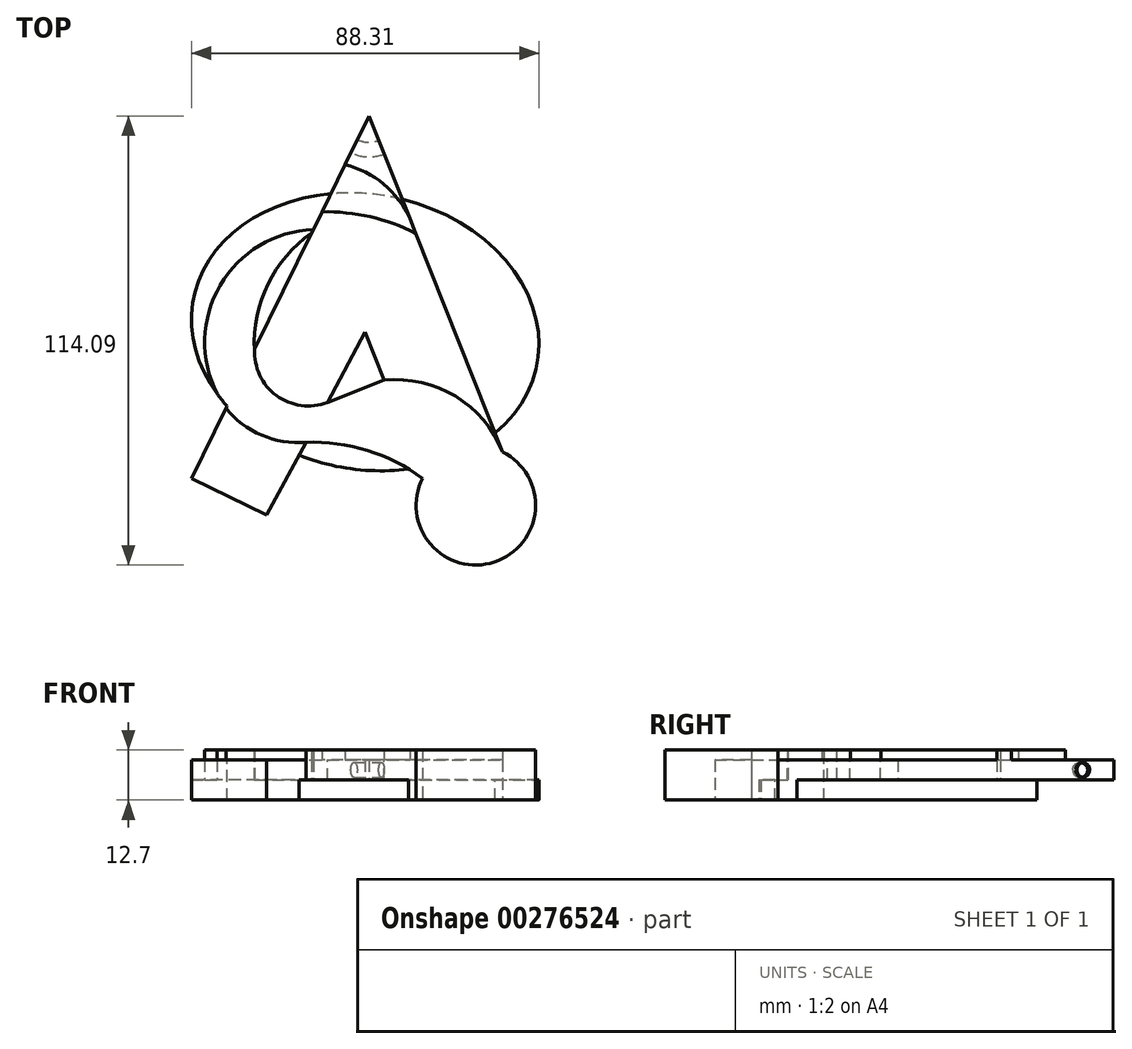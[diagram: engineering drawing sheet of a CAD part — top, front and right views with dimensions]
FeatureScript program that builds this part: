
annotation { "Feature Type Name" : "Feature", "Feature Type Description" : "" }
export const myFeature = defineFeature(function(context is Context, id is Id, definition is map)
    precondition{}
    {
        {
            var Q0;
            Q0=qCreatedBy(makeId("Top.planeOp"),FACE);
            var sketch = newSketch(context, id + "F0", { "sketchPlane" : qUnion([Q0])});
            skEllipse(sketch, "E0", {"center": v(-96.84, -32.47) * mm, "majorRadius": 44.45 * mm, "minorRadius": 34.93 * mm, "majorAxis": v(0.98, -0.19)});
            skSolve(sketch);
        }
        {
            var Q0;
            Q0=makeQuery(id+"F0.imprint","IMPRINT",FACE,{"disambiguationData":[TD([[makeQuery(id+"F0.imprint","IMPRINT",EDGE,{"derivedFrom":sQuery(id+"F0.wireOp",EDGE,"E0")}),1.0]])]});
            extrude(context, id + "F1", {"entities" : qUnion([Q0]), "depth" : 5.08 * mm});
        }
        {
            var Q0;
            Q0=makeQuery(id+"F1.opExtrude","CAP_FACE",FACE,{"disambiguationData":[OSD([sQuery(id+"F0.wireOp",EDGE,"E0")])],"isStart":false});
            var sketch = newSketch(context, id + "F2", { "sketchPlane" : qUnion([Q0])});
            skLineSegment(sketch, "E1", {"start": v(-140.96, -69.67) * mm, "end": v(-95.88, 22.4) * mm});
            skLineSegment(sketch, "E2", {"start": v(-95.88, 22.4) * mm, "end": v(-61.92, -63) * mm});
            skLineSegment(sketch, "E3", {"start": v(-140.96, -69.67) * mm, "end": v(-121.84, -79.03) * mm});
            skLineSegment(sketch, "E4", {"start": v(-121.84, -79.03) * mm, "end": v(-96.84, -32.47) * mm});
            skLineSegment(sketch, "E5", {"start": v(-96.84, -32.47) * mm, "end": v(-82.23, -69.67) * mm});
            skArc(sketch, "E6", {"start": v(-82.23, -69.67) * mm, "mid": v(-64, -90.95) * mm, "end": v(-61.92, -63) * mm});
            skSolve(sketch);
        }
        {
            var Q0;
            {var subQ0=sQuery(id+"F2.wireOp",EDGE,"E3");Q0=makeQuery(id+"F2.imprint","IMPRINT",FACE,{"disambiguationData":[TD([[makeQuery(id+"F2.imprint","IMPRINT",EDGE,{"derivedFrom":subQ0}),1.0]])]});}
            var Q1;
            {var subQ1=makeQuery(id+"F1.opExtrude","CAP_EDGE",EDGE,{"disambiguationData":[OSD([sQuery(id+"F0.wireOp",EDGE,"E0")])],"isStart":false});var subQ4=sQuery(id+"F2.wireOp",EDGE,"E1");var subQ11=makeQuery(id+"F2.imprint","INTERSECT",VERTEX,{"disambiguationData":[OD(0.0)],"derivedFrom":[subQ1,subQ4]});Q1=makeQuery(id+"F2.imprint","IMPRINT",FACE,{"disambiguationData":[TD([[makeQuery(id+"F2.imprint","IMPRINT",EDGE,{"disambiguationData":[TD([[subQ11,-1.0]])],"derivedFrom":subQ4}),-1.0]])]});}
            var Q2;
            {var subQ0=sQuery(id+"F2.wireOp",EDGE,"E6");Q2=makeQuery(id+"F2.imprint","IMPRINT",FACE,{"disambiguationData":[TD([[makeQuery(id+"F2.imprint","IMPRINT",EDGE,{"derivedFrom":subQ0}),1.0]])]});}
            var Q3;
            {var subQ0=sQuery(id+"F2.wireOp",EDGE,"E2");var subQ1=sQuery(id+"F2.wireOp",EDGE,"E1");var subQ2=makeQuery(id+"F2.imprint","INTERSECT",VERTEX,{"derivedFrom":[subQ1,subQ0]});Q3=makeQuery(id+"F2.imprint","IMPRINT",FACE,{"disambiguationData":[TD([[makeQuery(id+"F2.imprint","IMPRINT",EDGE,{"disambiguationData":[TD([[subQ2,1.0]])],"derivedFrom":subQ1}),-1.0]])]});}
            extrude(context, id + "F3", {"entities" : qUnion([Q0, Q1, Q2, Q3]), "operationType" : NewBodyOperationType.ADD, "depth" : 5.08 * mm});
        }
        {
            var Q0;
            Q0=makeQuery(id+"F3.opExtrude","CAP_FACE",FACE,{"disambiguationData":[OSD([sQuery(id+"F2.wireOp",EDGE,"E1"),sQuery(id+"F2.wireOp",EDGE,"E2"),sQuery(id+"F2.wireOp",EDGE,"E3"),sQuery(id+"F2.wireOp",EDGE,"E4"),sQuery(id+"F2.wireOp",EDGE,"E5"),sQuery(id+"F2.wireOp",EDGE,"E6")])],"isStart":false});
            var sketch = newSketch(context, id + "F4", { "sketchPlane" : qUnion([Q0])});
            skArc(sketch, "E7", {"start": v(-61.92, -63) * mm, "mid": v(-73.9, -48.83) * mm, "end": v(-92.01, -44.75) * mm});
            skLineSegment(sketch, "E8", {"start": v(-92.01, -44.75) * mm, "end": v(-106.45, -50.36) * mm});
            skArc(sketch, "E9", {"start": v(-124.88, -36.83) * mm, "mid": v(-119.38, -48.65) * mm, "end": v(-106.45, -50.36) * mm});
            skArc(sketch, "E10", {"start": v(-108.32, -3) * mm, "mid": v(-121.21, -17.66) * mm, "end": v(-124.88, -36.83) * mm});
            skArc(sketch, "E11", {"start": v(-108.32, -3) * mm, "mid": v(-133.14, -21.13) * mm, "end": v(-132.24, -51.85) * mm});
            skArc(sketch, "E12", {"start": v(-132.24, -51.85) * mm, "mid": v(-123.15, -58.72) * mm, "end": v(-111.9, -60.52) * mm});
            skArc(sketch, "E13", {"start": v(-82.23, -69.67) * mm, "mid": v(-96.3, -62.6) * mm, "end": v(-111.9, -60.52) * mm});
            skSolve(sketch);
        }
        {
            var Q0;
            {var subQ0=sQuery(id+"F4.wireOp",EDGE,"E7");Q0=makeQuery(id+"F4.imprint","IMPRINT",FACE,{"disambiguationData":[TD([[makeQuery(id+"F4.imprint","IMPRINT",EDGE,{"derivedFrom":subQ0}),1.0]])]});}
            var Q1;
            {var subQ0=sQuery(id+"F4.wireOp",EDGE,"E8");Q1=makeQuery(id+"F4.imprint","IMPRINT",FACE,{"disambiguationData":[TD([[makeQuery(id+"F4.imprint","IMPRINT",EDGE,{"derivedFrom":subQ0}),1.0]])]});}
            var Q2;
            {var subQ0=sQuery(id+"F4.wireOp",EDGE,"E9");Q2=makeQuery(id+"F4.imprint","IMPRINT",FACE,{"disambiguationData":[TD([[makeQuery(id+"F4.imprint","IMPRINT",EDGE,{"derivedFrom":subQ0}),-1.0]])]});}
            extrude(context, id + "F5", {"entities" : qUnion([Q0, Q1, Q2]), "operationType" : NewBodyOperationType.ADD, "depth" : 2.54 * mm});
        }
        {
            var Q0;
            {var subQ0=sQuery(id+"F0.wireOp",EDGE,"E0");var subQ1=sQuery(id+"F2.wireOp",EDGE,"E1");Q0=makeQuery(id+"F3.boolean.opBoolean","SPLIT",FACE,{"disambiguationData":[TD([makeQuery(id+"F3.opExtrude","SWEPT_FACE",FACE,{"disambiguationData":[OSD([subQ1])]})])],"derivedFrom":makeQuery(id+"F1.opExtrude","CAP_FACE",FACE,{"disambiguationData":[OSD([subQ0])],"isStart":false})});}
            var sketch = newSketch(context, id + "F6", { "sketchPlane" : qUnion([Q0])});
            skArc(sketch, "E14", {"start": v(-110.02, -6.47) * mm, "mid": v(-134.67, -22.53) * mm, "end": v(-132.24, -51.85) * mm});
            skArc(sketch, "E15", {"start": v(-110.45, -7.36) * mm, "mid": v(-121.54, -20.36) * mm, "end": v(-125, -37.08) * mm});
            skSolve(sketch);
        }
        {
            var Q0;
            Q0=makeQuery(id+"F5.opExtrude","CAP_FACE",FACE,{"disambiguationData":[OSD([sQuery(id+"F2.wireOp",EDGE,"E1"),sQuery(id+"F2.wireOp",EDGE,"E6"),sQuery(id+"F4.wireOp",EDGE,"E7"),sQuery(id+"F4.wireOp",EDGE,"E8"),sQuery(id+"F4.wireOp",EDGE,"E9"),sQuery(id+"F4.wireOp",EDGE,"E12"),sQuery(id+"F4.wireOp",EDGE,"E13")])],"isStart":true});
            extrude(context, id + "F7", {"entities" : qUnion([Q0]), "operationType" : NewBodyOperationType.ADD, "depth" : 10.16 * mm});
        }
        {
            var Q0;
            {var subQ0=sQuery(id+"F2.wireOp",EDGE,"E3");var subQ1=sQuery(id+"F0.wireOp",EDGE,"E0");var subQ2=sQuery(id+"F2.wireOp",EDGE,"E1");var subQ3=sQuery(id+"F2.wireOp",EDGE,"E4");Q0=makeQuery(id+"F3.boolean.opBoolean","SPLIT",FACE,{"disambiguationData":[TD([makeQuery(id+"F1.opExtrude","SWEPT_FACE",FACE,{"disambiguationData":[OSD([subQ1])]}),makeQuery(id+"F1.opExtrude","CAP_FACE",FACE,{"disambiguationData":[OSD([subQ1])],"isStart":false}),makeQuery(id+"F3.opExtrude","SWEPT_FACE",FACE,{"disambiguationData":[OSD([subQ2])]}),makeQuery(id+"F3.opExtrude","SWEPT_FACE",FACE,{"disambiguationData":[OSD([subQ0])]}),makeQuery(id+"F3.opExtrude","SWEPT_FACE",FACE,{"disambiguationData":[OSD([subQ3])]})])],"derivedFrom":makeQuery(id+"F3.opExtrude","CAP_FACE",FACE,{"disambiguationData":[OSD([subQ2,sQuery(id+"F2.wireOp",EDGE,"E2"),subQ0,subQ3,sQuery(id+"F2.wireOp",EDGE,"E5"),sQuery(id+"F2.wireOp",EDGE,"E6")])],"isStart":true})});}
            extrude(context, id + "F8", {"entities" : qUnion([Q0]), "operationType" : NewBodyOperationType.ADD, "depth" : 5.08 * mm});
        }
        {
            var Q0;
            {var subQ0=sQuery(id+"F2.wireOp",EDGE,"E5");var subQ1=sQuery(id+"F0.wireOp",EDGE,"E0");var subQ2=sQuery(id+"F2.wireOp",EDGE,"E2");var subQ3=sQuery(id+"F2.wireOp",EDGE,"E6");Q0=makeQuery(id+"F3.boolean.opBoolean","SPLIT",FACE,{"disambiguationData":[TD([makeQuery(id+"F1.opExtrude","SWEPT_FACE",FACE,{"disambiguationData":[OSD([subQ1])]}),makeQuery(id+"F1.opExtrude","CAP_FACE",FACE,{"disambiguationData":[OSD([subQ1])],"isStart":false}),makeQuery(id+"F3.opExtrude","SWEPT_FACE",FACE,{"disambiguationData":[OSD([subQ2])]}),makeQuery(id+"F3.opExtrude","SWEPT_FACE",FACE,{"disambiguationData":[OSD([subQ0])]}),makeQuery(id+"F3.opExtrude","SWEPT_FACE",FACE,{"disambiguationData":[OSD([subQ3])]})])],"derivedFrom":makeQuery(id+"F3.opExtrude","CAP_FACE",FACE,{"disambiguationData":[OSD([sQuery(id+"F2.wireOp",EDGE,"E1"),subQ2,sQuery(id+"F2.wireOp",EDGE,"E3"),sQuery(id+"F2.wireOp",EDGE,"E4"),subQ0,subQ3])],"isStart":true})});}
            extrude(context, id + "F9", {"entities" : qUnion([Q0]), "operationType" : NewBodyOperationType.ADD, "depth" : 5.08 * mm});
        }
        {
            var Q0;
            {var subQ0=sQuery(id+"F2.wireOp",EDGE,"E6");var subQ3=sQuery(id+"F2.wireOp",EDGE,"E1");var subQ5=sQuery(id+"F2.wireOp",EDGE,"E4");var subQ6=sQuery(id+"F2.wireOp",EDGE,"E2");var subQ7=sQuery(id+"F2.wireOp",EDGE,"E5");Q0=makeQuery(id+"F5.boolean.opBoolean","SPLIT",FACE,{"disambiguationData":[TD([makeQuery(id+"F3.opExtrude","SWEPT_FACE",FACE,{"disambiguationData":[OSD([subQ6])]})])],"derivedFrom":makeQuery(id+"F3.opExtrude","CAP_FACE",FACE,{"disambiguationData":[OSD([subQ3,subQ6,sQuery(id+"F2.wireOp",EDGE,"E3"),subQ5,subQ7,subQ0])],"isStart":false})});}
            var sketch = newSketch(context, id + "F10", { "sketchPlane" : qUnion([Q0])});
            skArc(sketch, "E16", {"start": v(-84.02, -7.43) * mm, "mid": v(-95.58, -3.23) * mm, "end": v(-107.81, -1.97) * mm});
            skPoint(sketch, "E17.end.orphan", {"position": v(-110.38, -7.22) * mm});
            skArc(sketch, "E18", {"start": v(-85.5, -3.72) * mm, "mid": v(-92.13, 5.05) * mm, "end": v(-101.95, 10) * mm});
            skSolve(sketch);
        }
        {
            var Q0;
            {var subQ7=sQuery(id+"F6.wireOp",EDGE,"E15");Q0=makeQuery(id+"F6.imprint","IMPRINT",FACE,{"disambiguationData":[TD([[makeQuery(id+"F6.imprint","IMPRINT",EDGE,{"derivedFrom":subQ7}),-1.0]])]});}
            extrude(context, id + "F11", {"entities" : qUnion([Q0]), "operationType" : NewBodyOperationType.ADD, "depth" : 7.62 * mm});
        }
        {
            var Q0;
            Q0 = qSketchRegion(id + "F10", true);
            var Q1;
            {var subQ0=sQuery(id+"F10.wireOp",EDGE,"E16");Q1=makeQuery(id+"F10.imprint","IMPRINT",FACE,{"disambiguationData":[TD([[makeQuery(id+"F10.imprint","IMPRINT",EDGE,{"derivedFrom":subQ0}),-1.0]])]});}
            extrude(context, id + "F12", {"entities" : qUnion([Q0, Q1]), "operationType" : NewBodyOperationType.ADD, "depth" : 2.54 * mm});
        }
        {
            var Q0;
            {var subQ0=sQuery(id+"F2.wireOp",EDGE,"E2");Q0=makeQuery(id+"F12.boolean.opBoolean","MERGE",FACE,{"derivedFrom":[makeQuery(id+"F9.boolean.opBoolean","MERGE",FACE,{"derivedFrom":[makeQuery(id+"F3.opExtrude","SWEPT_FACE",FACE,{"disambiguationData":[OSD([subQ0])]}),makeQuery(id+"F9.opExtrude","SWEPT_FACE",FACE,{"disambiguationData":[OSD([subQ0])]})]}),makeQuery(id+"F12.opExtrude","SWEPT_FACE",FACE,{"disambiguationData":[OSD([subQ0])]})]});}
            var sketch = newSketch(context, id + "F13", { "sketchPlane" : qUnion([Q0])});
            skCircle(sketch, "E19", {"center": v(47.65, 7.62) * mm, "radius": 1.9 * mm});
            skSolve(sketch);
        }
        {
            var Q0;
            Q0 = qSketchRegion(id + "F13", true);
            var Q1;
            Q1=makeQuery(id+"F3.opExtrude","SWEPT_EDGE",EDGE,{"disambiguationData":[OSD([sQuery(id+"F2.wireOp",EDGE,"E1"),sQuery(id+"F2.wireOp",EDGE,"E2")])]});
            revolve(context, id + "F14", {"operationType" : NewBodyOperationType.REMOVE, "entities" : qUnion([Q0]), "axis" : qUnion([Q1]), "revolveType" : RevolveType.FULL, "oppositeDirection" : true});
        }
    });
